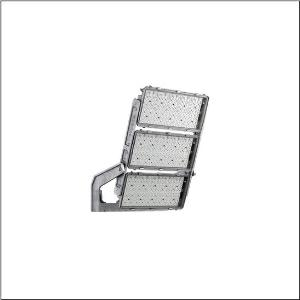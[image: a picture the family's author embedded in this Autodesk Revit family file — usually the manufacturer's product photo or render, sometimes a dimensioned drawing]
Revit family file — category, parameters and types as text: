
# Revit family: floodlight_fl_11_maxi_pro_remote___pl64blc_5xa779424w01aa_0c8b
name_source: partatom
category: Lighting Fixtures
units: mm (PartAtom-declared; Revit-internal decimal feet)

## family parameters
Cut with Voids When Loaded = No
Host = Face
Light Source = No
Part Type = Normal
Room Calculation Point = No
Round Connector Dimension = Use Diameter
Shared = No

## types (1)
- --- (1 x LED, 110040 lm, 1516.7 W, 5700K)
    Apparent Load = 1517 VA
    CIE Flux Codes = 28 83 99 100 100
    Color Rendering = 90
    Color Temperature = 5700K
    Default Elevation = 1800 mm
    Description = Floodlight FL 11  maxi  pro Remote floodlight; light control with lens of PMMA; cover panel of toughened safety glass, transparent; light distribution: PL64BLC, asymmetric direct distribution, LEDcolour temperature: 5700K, rated luminous flux: 110.040lm, colour rendering: CRI > 90, light colour: 957; luminous efficacy: 73lm/W; brightness control: DALI 2 (1 DALI address); with terminal, 8-pole, max. 2.5mm², mains connection: 220..240V/380..400V AC, 50/60Hz, surge voltage resistance: line to ground: 10kV, ECG replaceable separately, no afterglow with DALI off / DMX off command, LED unit replaceable without ESD environment, dustproof LED module, dimming range 10..100%; 1517W floodlight with 3x LED unit of diecast aluminium, coated grey; length: 1.003mm / width: 651mm / height: 338mm; mounting bracket, of diecast aluminium, uncoated, natural, equipment: Power, protection rating (complete): IP66; insulation class (complete): insulation class I (protective earthing); certification: CE; ball protection: ball impact resistance with accessories, impact resistance: IK07; only for outdoor installations, rated ambient temperature 10°C, permissible operating ambient temperature: -40..+30°C, permissible storage temperature: -40..+85°C; packaging unit: 1 piece

Light Distribution: PL64BLC
    Height = 320 mm
    Lamp = 1 x LED
    Lamp Light Flux = 110040 lm
    Lamp Power = 1516.7 W
    Lamp count = 1
    Length = 1002 mm
    Luminous efficacy = 73 lm/W
    Manufacturer = Siteco
    ModVariant = No
    Model = 5XA779424W01AA
    Mounting Place = Ceiling
    Mounting Type = Surface mounted
    Number of Poles = 1
    OnlyDefault = Yes
    Power Factor = 1
    Product Name = Floodlight FL 11 maxi pro Remote | PL64BLC
    Product group = floodlight | ceiling mounted
    ProductGroupID = 302
    Protection Class = Protection class I
    Protection Degree = IP 66
    RLX_Detail_Level = 1
    RLX_Emergency_Light_Flux = 0 lm
    RLX_Emergency_Type = 0
    RLX_Emergency_Type_DB = No
    RlxData = <blob elided: 52529 chars, md5=883d146e>
    Socket = socket
    Standby Power = 0 W
    System Light Flux = 110040 lm
    System Power = 1517 W
    Type Comments = factory setting: luminous flux: 100 % | dim-lin: 254 | 1070 mA
    Type Image = l_1006784.jpg
    URL = http://relux.com
    VarID = @adj_049511
    Voltage = 0 V
    Weight = 0.00 kg
    Width = 655 mm

## geometry (parser evidence)
native form markers: Blend x4, Sweep x14
no freeform markers — native parametric forms only
